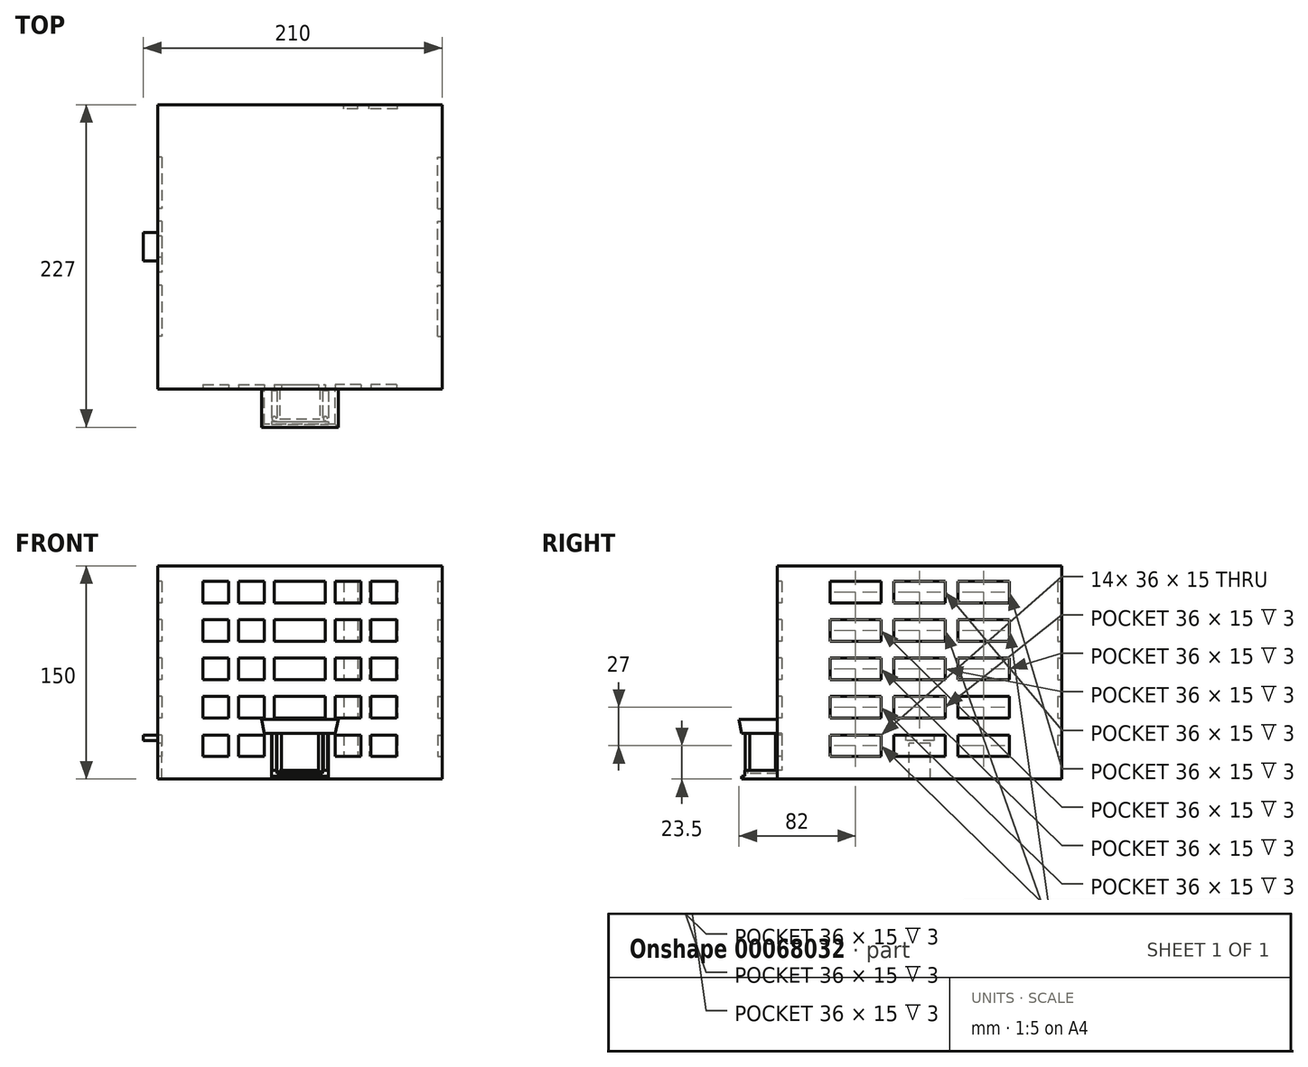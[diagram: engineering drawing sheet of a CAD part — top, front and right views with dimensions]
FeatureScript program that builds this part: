
annotation { "Feature Type Name" : "Feature", "Feature Type Description" : "" }
export const myFeature = defineFeature(function(context is Context, id is Id, definition is map)
    precondition{}
    {
        {
            var Q0;
            Q0=qCreatedBy(makeId("Top.planeOp"),FACE);
            var sketch = newSketch(context, id + "F0", { "sketchPlane" : qUnion([Q0])});
            skLineSegment(sketch, "E0.bottom", {"start": v(0, 0) * mm, "end": v(200, 0) * mm});
            skLineSegment(sketch, "E0.top", {"start": v(0, -200) * mm, "end": v(200, -200) * mm});
            skLineSegment(sketch, "E0.left", {"start": v(0, 0) * mm, "end": v(0, -200) * mm});
            skLineSegment(sketch, "E0.right", {"start": v(200, 0) * mm, "end": v(200, -200) * mm});
            skSolve(sketch);
        }
        {
            var Q0;
            Q0 = qSketchRegion(id + "F0", true);
            extrude(context, id + "F1", {"entities" : qUnion([Q0]), "depth" : 150 * mm});
        }
        {
            var Q0;
            Q0=qCreatedBy(makeId("Top.planeOp"),FACE);
            var sketch = newSketch(context, id + "F2", { "sketchPlane" : qUnion([Q0])});
            skLineSegment(sketch, "E1.bottom", {"start": v(80, -200) * mm, "end": v(120, -200) * mm});
            skLineSegment(sketch, "E1.top", {"start": v(80, -225) * mm, "end": v(120, -225) * mm});
            skLineSegment(sketch, "E1.left", {"start": v(80, -200) * mm, "end": v(80, -225) * mm});
            skLineSegment(sketch, "E1.right", {"start": v(120, -200) * mm, "end": v(120, -225) * mm});
            skSolve(sketch);
        }
        {
            var Q0;
            Q0=makeQuery(id+"F2.imprint","IMPRINT",FACE,{"disambiguationData":[TD([[makeQuery(id+"F2.imprint","IMPRINT",EDGE,{"derivedFrom":sQuery(id+"F2.wireOp",EDGE,"E1.bottom")}),-1.0]])]});
            extrude(context, id + "F3", {"entities" : qUnion([Q0]), "operationType" : NewBodyOperationType.ADD, "depth" : 2 * mm});
        }
        {
            var Q0;
            Q0=makeQuery(id+"F3.opExtrude","CAP_FACE",FACE,{"disambiguationData":[OSD([sQuery(id+"F2.wireOp",EDGE,"E1.bottom"),sQuery(id+"F2.wireOp",EDGE,"E1.top"),sQuery(id+"F2.wireOp",EDGE,"E1.left"),sQuery(id+"F2.wireOp",EDGE,"E1.right")])],"isStart":false});
            var sketch = newSketch(context, id + "F4", { "sketchPlane" : qUnion([Q0])});
            skLineSegment(sketch, "E2.bottom", {"start": v(84, -200) * mm, "end": v(116, -200) * mm});
            skLineSegment(sketch, "E2.top", {"start": v(84, -223) * mm, "end": v(116, -223) * mm});
            skLineSegment(sketch, "E2.left", {"start": v(84, -200) * mm, "end": v(84, -223) * mm});
            skLineSegment(sketch, "E2.right", {"start": v(116, -200) * mm, "end": v(116, -223) * mm});
            skSolve(sketch);
        }
        {
            var Q0;
            Q0=makeQuery(id+"F4.imprint","IMPRINT",FACE,{"disambiguationData":[TD([[makeQuery(id+"F4.imprint","IMPRINT",EDGE,{"derivedFrom":sQuery(id+"F4.wireOp",EDGE,"E2.bottom")}),-1.0]])]});
            extrude(context, id + "F5", {"entities" : qUnion([Q0]), "operationType" : NewBodyOperationType.ADD, "depth" : 2 * mm});
        }
        {
            var Q0;
            Q0=makeQuery(id+"F5.opExtrude","CAP_FACE",FACE,{"disambiguationData":[OSD([sQuery(id+"F4.wireOp",EDGE,"E2.bottom"),sQuery(id+"F4.wireOp",EDGE,"E2.top"),sQuery(id+"F4.wireOp",EDGE,"E2.left"),sQuery(id+"F4.wireOp",EDGE,"E2.right")])],"isStart":false});
            var sketch = newSketch(context, id + "F6", { "sketchPlane" : qUnion([Q0])});
            skLineSegment(sketch, "E3.bottom", {"start": v(86, -200) * mm, "end": v(114, -200) * mm});
            skLineSegment(sketch, "E3.top", {"start": v(86, -221) * mm, "end": v(114, -221) * mm});
            skLineSegment(sketch, "E3.left", {"start": v(86, -200) * mm, "end": v(86, -221) * mm});
            skLineSegment(sketch, "E3.right", {"start": v(114, -200) * mm, "end": v(114, -221) * mm});
            skSolve(sketch);
        }
        {
            var Q0;
            Q0=makeQuery(id+"F6.imprint","IMPRINT",FACE,{"disambiguationData":[TD([[makeQuery(id+"F6.imprint","IMPRINT",EDGE,{"derivedFrom":sQuery(id+"F6.wireOp",EDGE,"E3.bottom")}),-1.0]])]});
            extrude(context, id + "F7", {"entities" : qUnion([Q0]), "operationType" : NewBodyOperationType.ADD, "depth" : 2 * mm});
        }
        {
            var Q0;
            Q0=makeQuery(id+"F3.opExtrude","CAP_FACE",FACE,{"disambiguationData":[OSD([sQuery(id+"F2.wireOp",EDGE,"E1.bottom"),sQuery(id+"F2.wireOp",EDGE,"E1.top"),sQuery(id+"F2.wireOp",EDGE,"E1.left"),sQuery(id+"F2.wireOp",EDGE,"E1.right")])],"isStart":false});
            var sketch = newSketch(context, id + "F8", { "sketchPlane" : qUnion([Q0])});
            skLineSegment(sketch, "E4.bottom", {"start": v(84, -223) * mm, "end": v(80, -223) * mm});
            skLineSegment(sketch, "E4.top", {"start": v(84, -200) * mm, "end": v(80, -200) * mm});
            skLineSegment(sketch, "E4.left", {"start": v(84, -223) * mm, "end": v(84, -200) * mm});
            skLineSegment(sketch, "E4.right", {"start": v(80, -223) * mm, "end": v(80, -200) * mm});
            skLineSegment(sketch, "E5.bottom", {"start": v(116, -200) * mm, "end": v(120, -200) * mm});
            skLineSegment(sketch, "E5.top", {"start": v(116, -223) * mm, "end": v(120, -223) * mm});
            skLineSegment(sketch, "E5.left", {"start": v(116, -200) * mm, "end": v(116, -223) * mm});
            skLineSegment(sketch, "E5.right", {"start": v(120, -200) * mm, "end": v(120, -223) * mm});
            skSolve(sketch);
        }
        {
            var Q0;
            Q0 = qSketchRegion(id + "F8", true);
            extrude(context, id + "F9", {"entities" : qUnion([Q0]), "operationType" : NewBodyOperationType.ADD, "depth" : 4 * mm});
        }
        {
            var Q0;
            Q0=makeQuery(id+"F9.opExtrude","CAP_FACE",FACE,{"disambiguationData":[OSD([sQuery(id+"F8.wireOp",EDGE,"E4.bottom"),sQuery(id+"F8.wireOp",EDGE,"E4.top"),sQuery(id+"F8.wireOp",EDGE,"E4.left"),sQuery(id+"F8.wireOp",EDGE,"E4.right")])],"isStart":false});
            var sketch = newSketch(context, id + "F10", { "sketchPlane" : qUnion([Q0])});
            skCircle(sketch, "E6", {"center": v(82, -221) * mm, "radius": 1.5 * mm});
            skCircle(sketch, "E7", {"center": v(118, -221) * mm, "radius": 1.5 * mm});
            skSolve(sketch);
        }
        {
            var Q0;
            Q0 = qSketchRegion(id + "F10", true);
            extrude(context, id + "F11", {"entities" : qUnion([Q0]), "operationType" : NewBodyOperationType.ADD, "depth" : 26 * mm});
        }
        {
            var Q0;
            Q0=makeQuery(id+"F11.opExtrude","CAP_FACE",FACE,{"disambiguationData":[OSD([sQuery(id+"F10.wireOp",EDGE,"E7")])],"isStart":false});
            var sketch = newSketch(context, id + "F12", { "sketchPlane" : qUnion([Q0])});
            skLineSegment(sketch, "E8.bottom", {"start": v(125, -225) * mm, "end": v(75, -225) * mm});
            skLineSegment(sketch, "E8.top", {"start": v(125, -200) * mm, "end": v(75, -200) * mm});
            skLineSegment(sketch, "E8.left", {"start": v(125, -225) * mm, "end": v(125, -200) * mm});
            skLineSegment(sketch, "E8.right", {"start": v(75, -225) * mm, "end": v(75, -200) * mm});
            skSolve(sketch);
        }
        {
            var Q0;
            Q0=makeQuery(id+"F12.imprint","IMPRINT",FACE,{"disambiguationData":[TD([[makeQuery(id+"F12.imprint","IMPRINT",EDGE,{"derivedFrom":sQuery(id+"F12.wireOp",EDGE,"E8.bottom")}),-1.0]])]});
            cPlane(context, id + "F13", {"entities" : qUnion([Q0]), "cplaneType" : CPlaneType.OFFSET, "offset" : 10 * mm, "width" : 150 * mm, "height" : 150 * mm});
        }
        {
            var Q0;
            Q0=qCreatedBy(id+"F13.planeOp",FACE);
            var sketch = newSketch(context, id + "F14", { "sketchPlane" : qUnion([Q0])});
            skLineSegment(sketch, "E9.bottom", {"start": v(73, -200) * mm, "end": v(127, -200) * mm});
            skLineSegment(sketch, "E9.top", {"start": v(73, -227) * mm, "end": v(127, -227) * mm});
            skLineSegment(sketch, "E9.left", {"start": v(73, -200) * mm, "end": v(73, -227) * mm});
            skLineSegment(sketch, "E9.right", {"start": v(127, -200) * mm, "end": v(127, -227) * mm});
            skSolve(sketch);
        }
        {
            var Q1;
            Q1 = qSketchRegion(id + "F14", true);
            var Q2;
            Q2 = qSketchRegion(id + "F12", true);
            loft(context, id + "F15", {"operationType" : NewBodyOperationType.ADD, "sheetProfilesArray" : [{ "sheetProfileEntities" : qUnion([Q1]) }, { "sheetProfileEntities" : qUnion([Q2]) }]});
        }
        {
            var Q0;
            Q0=makeQuery(id+"F1.opExtrude","SWEPT_FACE",FACE,{"disambiguationData":[OSD([sQuery(id+"F0.wireOp",EDGE,"E0.top")])]});
            var sketch = newSketch(context, id + "F16", { "sketchPlane" : qUnion([Q0])});
            skLineSegment(sketch, "E10.bottom", {"start": v(84, 6) * mm, "end": v(80, 6) * mm});
            skLineSegment(sketch, "E10.top", {"start": v(84, 32) * mm, "end": v(80, 32) * mm});
            skLineSegment(sketch, "E10.left", {"start": v(84, 6) * mm, "end": v(84, 32) * mm});
            skLineSegment(sketch, "E10.right", {"start": v(80, 6) * mm, "end": v(80, 32) * mm});
            skLineSegment(sketch, "E11.bottom", {"start": v(116, 6) * mm, "end": v(120, 6) * mm});
            skLineSegment(sketch, "E11.top", {"start": v(116, 32) * mm, "end": v(120, 32) * mm});
            skLineSegment(sketch, "E11.left", {"start": v(116, 6) * mm, "end": v(116, 32) * mm});
            skLineSegment(sketch, "E11.right", {"start": v(120, 6) * mm, "end": v(120, 32) * mm});
            skSolve(sketch);
        }
        {
            var Q0;
            Q0 = qSketchRegion(id + "F16", true);
            extrude(context, id + "F17", {"entities" : qUnion([Q0]), "operationType" : NewBodyOperationType.ADD, "depth" : 1.5 * mm});
        }
        {
            var Q0;
            {var subQ7=sQuery(id+"F0.wireOp",EDGE,"E0.left");var subQ11=sQuery(id+"F0.wireOp",EDGE,"E0.top");Q0=makeQuery(id+"F17.boolean.opBoolean","SPLIT",FACE,{"disambiguationData":[TD([makeQuery(id+"F1.opExtrude","SWEPT_FACE",FACE,{"disambiguationData":[OSD([subQ7])]})])],"derivedFrom":makeQuery(id+"F1.opExtrude","SWEPT_FACE",FACE,{"disambiguationData":[OSD([subQ11])]})});}
            var sketch = newSketch(context, id + "F18", { "sketchPlane" : qUnion([Q0])});
            skLineSegment(sketch, "E12.bottom", {"start": v(32, 139) * mm, "end": v(50, 139) * mm});
            skLineSegment(sketch, "E12.top", {"start": v(32, 124) * mm, "end": v(50, 124) * mm});
            skLineSegment(sketch, "E12.left", {"start": v(32, 139) * mm, "end": v(32, 124) * mm});
            skLineSegment(sketch, "E12.right", {"start": v(50, 139) * mm, "end": v(50, 124) * mm});
            skLineSegment(sketch, "E13.0.1.0", {"start": v(32, 112) * mm, "end": v(50, 112) * mm});
            skLineSegment(sketch, "E13.0.1.1", {"start": v(32, 97) * mm, "end": v(50, 97) * mm});
            skLineSegment(sketch, "E13.0.1.2", {"start": v(32, 112) * mm, "end": v(32, 97) * mm});
            skLineSegment(sketch, "E13.0.1.3", {"start": v(50, 112) * mm, "end": v(50, 97) * mm});
            skLineSegment(sketch, "E13.0.2.0", {"start": v(32, 85) * mm, "end": v(50, 85) * mm});
            skLineSegment(sketch, "E13.0.2.1", {"start": v(32, 70) * mm, "end": v(50, 70) * mm});
            skLineSegment(sketch, "E13.0.2.2", {"start": v(32, 85) * mm, "end": v(32, 70) * mm});
            skLineSegment(sketch, "E13.0.2.3", {"start": v(50, 85) * mm, "end": v(50, 70) * mm});
            skLineSegment(sketch, "E13.0.3.0", {"start": v(32, 58) * mm, "end": v(50, 58) * mm});
            skLineSegment(sketch, "E13.0.3.1", {"start": v(32, 43) * mm, "end": v(50, 43) * mm});
            skLineSegment(sketch, "E13.0.3.2", {"start": v(32, 58) * mm, "end": v(32, 43) * mm});
            skLineSegment(sketch, "E13.0.3.3", {"start": v(50, 58) * mm, "end": v(50, 43) * mm});
            skLineSegment(sketch, "E13.0.4.0", {"start": v(32, 31) * mm, "end": v(50, 31) * mm});
            skLineSegment(sketch, "E13.0.4.1", {"start": v(32, 16) * mm, "end": v(50, 16) * mm});
            skLineSegment(sketch, "E13.0.4.2", {"start": v(32, 31) * mm, "end": v(32, 16) * mm});
            skLineSegment(sketch, "E13.0.4.3", {"start": v(50, 31) * mm, "end": v(50, 16) * mm});
            skLineSegment(sketch, "E13.1.0.0", {"start": v(57, 139) * mm, "end": v(75, 139) * mm});
            skLineSegment(sketch, "E13.1.0.1", {"start": v(57, 124) * mm, "end": v(75, 124) * mm});
            skLineSegment(sketch, "E13.1.0.2", {"start": v(57, 139) * mm, "end": v(57, 124) * mm});
            skLineSegment(sketch, "E13.1.0.3", {"start": v(75, 139) * mm, "end": v(75, 124) * mm});
            skLineSegment(sketch, "E13.1.1.0", {"start": v(57, 112) * mm, "end": v(75, 112) * mm});
            skLineSegment(sketch, "E13.1.1.1", {"start": v(57, 97) * mm, "end": v(75, 97) * mm});
            skLineSegment(sketch, "E13.1.1.2", {"start": v(57, 112) * mm, "end": v(57, 97) * mm});
            skLineSegment(sketch, "E13.1.1.3", {"start": v(75, 112) * mm, "end": v(75, 97) * mm});
            skLineSegment(sketch, "E13.1.2.0", {"start": v(57, 85) * mm, "end": v(75, 85) * mm});
            skLineSegment(sketch, "E13.1.2.1", {"start": v(57, 70) * mm, "end": v(75, 70) * mm});
            skLineSegment(sketch, "E13.1.2.2", {"start": v(57, 85) * mm, "end": v(57, 70) * mm});
            skLineSegment(sketch, "E13.1.2.3", {"start": v(75, 85) * mm, "end": v(75, 70) * mm});
            skLineSegment(sketch, "E13.1.3.0", {"start": v(57, 58) * mm, "end": v(75, 58) * mm});
            skLineSegment(sketch, "E13.1.3.1", {"start": v(57, 43) * mm, "end": v(75, 43) * mm});
            skLineSegment(sketch, "E13.1.3.2", {"start": v(57, 58) * mm, "end": v(57, 43) * mm});
            skLineSegment(sketch, "E13.1.3.3", {"start": v(75, 58) * mm, "end": v(75, 43) * mm});
            skLineSegment(sketch, "E13.1.4.0", {"start": v(57, 31) * mm, "end": v(75, 31) * mm});
            skLineSegment(sketch, "E13.1.4.1", {"start": v(57, 16) * mm, "end": v(75, 16) * mm});
            skLineSegment(sketch, "E13.1.4.2", {"start": v(57, 31) * mm, "end": v(57, 16) * mm});
            skLineSegment(sketch, "E13.1.4.3", {"start": v(75, 31) * mm, "end": v(75, 16) * mm});
            skLineSegment(sketch, "E13.2.0.0", {"start": v(82, 139) * mm, "end": v(100, 139) * mm});
            skLineSegment(sketch, "E13.2.0.1", {"start": v(82, 124) * mm, "end": v(100, 124) * mm});
            skLineSegment(sketch, "E13.2.0.2", {"start": v(82, 139) * mm, "end": v(82, 124) * mm});
            skLineSegment(sketch, "E13.2.0.3", {"start": v(100, 139) * mm, "end": v(100, 124) * mm});
            skLineSegment(sketch, "E13.2.1.0", {"start": v(82, 112) * mm, "end": v(100, 112) * mm});
            skLineSegment(sketch, "E13.2.1.1", {"start": v(82, 97) * mm, "end": v(100, 97) * mm});
            skLineSegment(sketch, "E13.2.1.2", {"start": v(82, 112) * mm, "end": v(82, 97) * mm});
            skLineSegment(sketch, "E13.2.1.3", {"start": v(100, 112) * mm, "end": v(100, 97) * mm});
            skLineSegment(sketch, "E13.2.2.0", {"start": v(82, 85) * mm, "end": v(100, 85) * mm});
            skLineSegment(sketch, "E13.2.2.1", {"start": v(82, 70) * mm, "end": v(100, 70) * mm});
            skLineSegment(sketch, "E13.2.2.2", {"start": v(82, 85) * mm, "end": v(82, 70) * mm});
            skLineSegment(sketch, "E13.2.2.3", {"start": v(100, 85) * mm, "end": v(100, 70) * mm});
            skLineSegment(sketch, "E13.2.3.0", {"start": v(82, 58) * mm, "end": v(100, 58) * mm});
            skLineSegment(sketch, "E13.2.3.1", {"start": v(82, 43) * mm, "end": v(100, 43) * mm});
            skLineSegment(sketch, "E13.2.3.2", {"start": v(82, 58) * mm, "end": v(82, 43) * mm});
            skLineSegment(sketch, "E13.2.3.3", {"start": v(100, 58) * mm, "end": v(100, 43) * mm});
            skLineSegment(sketch, "E13.direction1", {"start": v(32, 139) * mm, "end": v(57, 139) * mm, "construction": true});
            skLineSegment(sketch, "E13.direction2", {"start": v(32, 139) * mm, "end": v(32, 112) * mm, "construction": true});
            skLineSegment(sketch, "E14", {"start": v(100, 150) * mm, "end": v(100, -27.9) * mm, "construction": true});
            skLineSegment(sketch, "E15.MirrorCS", {"start": v(125, 85) * mm, "end": v(125, 70) * mm});
            skLineSegment(sketch, "E16.MirrorCS", {"start": v(118, 58) * mm, "end": v(118, 43) * mm});
            skLineSegment(sketch, "E17.MirrorCS", {"start": v(143, 31) * mm, "end": v(143, 16) * mm});
            skLineSegment(sketch, "E18.MirrorCS", {"start": v(143, 139) * mm, "end": v(143, 124) * mm});
            skLineSegment(sketch, "E19.MirrorCS", {"start": v(143, 85) * mm, "end": v(125, 85) * mm});
            skLineSegment(sketch, "E20.MirrorCS", {"start": v(118, 112) * mm, "end": v(100, 112) * mm});
            skLineSegment(sketch, "E21.MirrorCS", {"start": v(168, 58) * mm, "end": v(150, 58) * mm});
            skLineSegment(sketch, "E22.MirrorCS", {"start": v(150, 85) * mm, "end": v(150, 70) * mm});
            skLineSegment(sketch, "E23.MirrorCS", {"start": v(168, 85) * mm, "end": v(168, 70) * mm});
            skLineSegment(sketch, "E24.MirrorCS", {"start": v(168, 70) * mm, "end": v(150, 70) * mm});
            skLineSegment(sketch, "E25.MirrorCS", {"start": v(168, 85) * mm, "end": v(150, 85) * mm});
            skLineSegment(sketch, "E26.MirrorCS", {"start": v(150, 112) * mm, "end": v(150, 97) * mm});
            skLineSegment(sketch, "E27.MirrorCS", {"start": v(168, 112) * mm, "end": v(168, 97) * mm});
            skLineSegment(sketch, "E28.MirrorCS", {"start": v(168, 97) * mm, "end": v(150, 97) * mm});
            skLineSegment(sketch, "E29.MirrorCS", {"start": v(168, 112) * mm, "end": v(150, 112) * mm});
            skLineSegment(sketch, "E30.MirrorCS", {"start": v(150, 139) * mm, "end": v(150, 124) * mm});
            skLineSegment(sketch, "E31.MirrorCS", {"start": v(168, 139) * mm, "end": v(168, 124) * mm});
            skLineSegment(sketch, "E32.MirrorCS", {"start": v(168, 124) * mm, "end": v(150, 124) * mm});
            skLineSegment(sketch, "E33.MirrorCS", {"start": v(150, 58) * mm, "end": v(150, 43) * mm});
            skLineSegment(sketch, "E34.MirrorCS", {"start": v(168, 139) * mm, "end": v(150, 139) * mm});
            skLineSegment(sketch, "E35.MirrorCS", {"start": v(143, 16) * mm, "end": v(125, 16) * mm});
            skLineSegment(sketch, "E36.MirrorCS", {"start": v(143, 85) * mm, "end": v(143, 70) * mm});
            skLineSegment(sketch, "E37.MirrorCS", {"start": v(118, 112) * mm, "end": v(118, 97) * mm});
            skLineSegment(sketch, "E38.MirrorCS", {"start": v(118, 43) * mm, "end": v(100, 43) * mm});
            skLineSegment(sketch, "E39.MirrorCS", {"start": v(168, 58) * mm, "end": v(168, 43) * mm});
            skLineSegment(sketch, "E40.MirrorCS", {"start": v(143, 124) * mm, "end": v(125, 124) * mm});
            skLineSegment(sketch, "E41.MirrorCS", {"start": v(125, 112) * mm, "end": v(125, 97) * mm});
            skLineSegment(sketch, "E42.MirrorCS", {"start": v(168, 43) * mm, "end": v(150, 43) * mm});
            skLineSegment(sketch, "E43.MirrorCS", {"start": v(143, 70) * mm, "end": v(125, 70) * mm});
            skLineSegment(sketch, "E44.MirrorCS", {"start": v(143, 31) * mm, "end": v(125, 31) * mm});
            skLineSegment(sketch, "E45.MirrorCS", {"start": v(118, 58) * mm, "end": v(100, 58) * mm});
            skLineSegment(sketch, "E46.MirrorCS", {"start": v(118, 97) * mm, "end": v(100, 97) * mm});
            skLineSegment(sketch, "E47.MirrorCS", {"start": v(143, 112) * mm, "end": v(143, 97) * mm});
            skLineSegment(sketch, "E48.MirrorCS", {"start": v(143, 139) * mm, "end": v(125, 139) * mm});
            skLineSegment(sketch, "E49.MirrorCS", {"start": v(118, 139) * mm, "end": v(118, 124) * mm});
            skLineSegment(sketch, "E50.MirrorCS", {"start": v(125, 58) * mm, "end": v(125, 43) * mm});
            skLineSegment(sketch, "E51.MirrorCS", {"start": v(150, 31) * mm, "end": v(150, 16) * mm});
            skLineSegment(sketch, "E52.MirrorCS", {"start": v(143, 97) * mm, "end": v(125, 97) * mm});
            skLineSegment(sketch, "E53.MirrorCS", {"start": v(168, 139) * mm, "end": v(168, 112) * mm, "construction": true});
            skLineSegment(sketch, "E54.MirrorCS", {"start": v(118, 124) * mm, "end": v(100, 124) * mm});
            skLineSegment(sketch, "E55.MirrorCS", {"start": v(143, 58) * mm, "end": v(143, 43) * mm});
            skLineSegment(sketch, "E56.MirrorCS", {"start": v(118, 85) * mm, "end": v(118, 70) * mm});
            skLineSegment(sketch, "E57.MirrorCS", {"start": v(168, 31) * mm, "end": v(168, 16) * mm});
            skLineSegment(sketch, "E58.MirrorCS", {"start": v(143, 112) * mm, "end": v(125, 112) * mm});
            skLineSegment(sketch, "E59.MirrorCS", {"start": v(118, 139) * mm, "end": v(100, 139) * mm});
            skLineSegment(sketch, "E60.MirrorCS", {"start": v(168, 139) * mm, "end": v(143, 139) * mm, "construction": true});
            skLineSegment(sketch, "E61.MirrorCS", {"start": v(143, 43) * mm, "end": v(125, 43) * mm});
            skLineSegment(sketch, "E62.MirrorCS", {"start": v(118, 70) * mm, "end": v(100, 70) * mm});
            skLineSegment(sketch, "E63.MirrorCS", {"start": v(168, 16) * mm, "end": v(150, 16) * mm});
            skLineSegment(sketch, "E64.MirrorCS", {"start": v(143, 58) * mm, "end": v(125, 58) * mm});
            skLineSegment(sketch, "E65.MirrorCS", {"start": v(118, 85) * mm, "end": v(100, 85) * mm});
            skLineSegment(sketch, "E66.MirrorCS", {"start": v(125, 139) * mm, "end": v(125, 124) * mm});
            skLineSegment(sketch, "E67.MirrorCS", {"start": v(168, 31) * mm, "end": v(150, 31) * mm});
            skLineSegment(sketch, "E68.MirrorCS", {"start": v(125, 31) * mm, "end": v(125, 16) * mm});
            skLineSegment(sketch, "E69.bottom", {"start": v(87, 32) * mm, "end": v(113, 32) * mm});
            skLineSegment(sketch, "E69.top", {"start": v(87, 6) * mm, "end": v(113, 6) * mm});
            skLineSegment(sketch, "E69.left", {"start": v(87, 32) * mm, "end": v(87, 6) * mm});
            skLineSegment(sketch, "E69.right", {"start": v(113, 32) * mm, "end": v(113, 6) * mm});
            skSolve(sketch);
        }
        {
            var Q0;
            Q0 = qSketchRegion(id + "F18", true);
            extrude(context, id + "F19", {"entities" : qUnion([Q0]), "operationType" : NewBodyOperationType.REMOVE, "oppositeDirection" : true, "depth" : 3 * mm});
        }
        {
            var Q0;
            Q0=makeQuery(id+"F1.opExtrude","SWEPT_FACE",FACE,{"disambiguationData":[OSD([sQuery(id+"F0.wireOp",EDGE,"E0.right")])]});
            var sketch = newSketch(context, id + "F20", { "sketchPlane" : qUnion([Q0])});
            skLineSegment(sketch, "E70.bottom", {"start": v(-163, 139) * mm, "end": v(-127, 139) * mm});
            skLineSegment(sketch, "E70.top", {"start": v(-163, 124) * mm, "end": v(-127, 124) * mm});
            skLineSegment(sketch, "E70.left", {"start": v(-163, 139) * mm, "end": v(-163, 124) * mm});
            skLineSegment(sketch, "E70.right", {"start": v(-127, 139) * mm, "end": v(-127, 124) * mm});
            skLineSegment(sketch, "E71.direction1", {"start": v(-127, 124) * mm, "end": v(-82, 124) * mm, "construction": true});
            skLineSegment(sketch, "E72.0.1.0", {"start": v(-82, 139) * mm, "end": v(-82, 124) * mm});
            skLineSegment(sketch, "E72.3.1.0", {"start": v(-118, 139) * mm, "end": v(-118, 124) * mm});
            skLineSegment(sketch, "E72.6.1.0", {"start": v(-118, 124) * mm, "end": v(-82, 124) * mm});
            skLineSegment(sketch, "E72.9.1.0", {"start": v(-118, 139) * mm, "end": v(-82, 139) * mm});
            skLineSegment(sketch, "E72.0.2.0", {"start": v(-37, 139) * mm, "end": v(-37, 124) * mm});
            skLineSegment(sketch, "E72.3.2.0", {"start": v(-73, 139) * mm, "end": v(-73, 124) * mm});
            skLineSegment(sketch, "E72.6.2.0", {"start": v(-73, 124) * mm, "end": v(-37, 124) * mm});
            skLineSegment(sketch, "E72.9.2.0", {"start": v(-73, 139) * mm, "end": v(-37, 139) * mm});
            skLineSegment(sketch, "E73.0.1.0", {"start": v(-127, 112) * mm, "end": v(-127, 97) * mm});
            skLineSegment(sketch, "E73.0.1.1", {"start": v(-163, 112) * mm, "end": v(-163, 97) * mm});
            skLineSegment(sketch, "E73.0.1.2", {"start": v(-163, 97) * mm, "end": v(-127, 97) * mm});
            skLineSegment(sketch, "E73.0.1.3", {"start": v(-163, 112) * mm, "end": v(-127, 112) * mm});
            skLineSegment(sketch, "E73.0.1.4", {"start": v(-127, 97) * mm, "end": v(-82, 97) * mm, "construction": true});
            skLineSegment(sketch, "E73.0.2.0", {"start": v(-127, 85) * mm, "end": v(-127, 70) * mm});
            skLineSegment(sketch, "E73.0.2.1", {"start": v(-163, 85) * mm, "end": v(-163, 70) * mm});
            skLineSegment(sketch, "E73.0.2.2", {"start": v(-163, 70) * mm, "end": v(-127, 70) * mm});
            skLineSegment(sketch, "E73.0.2.3", {"start": v(-163, 85) * mm, "end": v(-127, 85) * mm});
            skLineSegment(sketch, "E73.0.2.4", {"start": v(-127, 70) * mm, "end": v(-82, 70) * mm, "construction": true});
            skLineSegment(sketch, "E73.0.3.0", {"start": v(-127, 58) * mm, "end": v(-127, 43) * mm});
            skLineSegment(sketch, "E73.0.3.1", {"start": v(-163, 58) * mm, "end": v(-163, 43) * mm});
            skLineSegment(sketch, "E73.0.3.2", {"start": v(-163, 43) * mm, "end": v(-127, 43) * mm});
            skLineSegment(sketch, "E73.0.3.3", {"start": v(-163, 58) * mm, "end": v(-127, 58) * mm});
            skLineSegment(sketch, "E73.0.3.4", {"start": v(-127, 43) * mm, "end": v(-82, 43) * mm, "construction": true});
            skLineSegment(sketch, "E73.0.4.0", {"start": v(-127, 31) * mm, "end": v(-127, 16) * mm});
            skLineSegment(sketch, "E73.0.4.1", {"start": v(-163, 31) * mm, "end": v(-163, 16) * mm});
            skLineSegment(sketch, "E73.0.4.2", {"start": v(-163, 16) * mm, "end": v(-127, 16) * mm});
            skLineSegment(sketch, "E73.0.4.3", {"start": v(-163, 31) * mm, "end": v(-127, 31) * mm});
            skLineSegment(sketch, "E73.0.4.4", {"start": v(-127, 16) * mm, "end": v(-82, 16) * mm, "construction": true});
            skLineSegment(sketch, "E73.direction1", {"start": v(-118, 139) * mm, "end": v(-93, 139) * mm, "construction": true});
            skLineSegment(sketch, "E73.direction2", {"start": v(-118, 139) * mm, "end": v(-118, 112) * mm, "construction": true});
            skLineSegment(sketch, "E74.0.1.0", {"start": v(-118, 97) * mm, "end": v(-82, 97) * mm});
            skLineSegment(sketch, "E74.0.1.1", {"start": v(-118, 112) * mm, "end": v(-118, 97) * mm});
            skLineSegment(sketch, "E74.0.1.2", {"start": v(-82, 112) * mm, "end": v(-82, 97) * mm});
            skLineSegment(sketch, "E74.0.1.3", {"start": v(-73, 97) * mm, "end": v(-37, 97) * mm});
            skLineSegment(sketch, "E74.0.1.4", {"start": v(-73, 112) * mm, "end": v(-73, 97) * mm});
            skLineSegment(sketch, "E74.0.1.5", {"start": v(-37, 112) * mm, "end": v(-37, 97) * mm});
            skLineSegment(sketch, "E74.0.1.6", {"start": v(-73, 112) * mm, "end": v(-37, 112) * mm});
            skLineSegment(sketch, "E74.0.1.7", {"start": v(-118, 112) * mm, "end": v(-82, 112) * mm});
            skLineSegment(sketch, "E74.0.1.8", {"start": v(-118, 112) * mm, "end": v(-93, 112) * mm, "construction": true});
            skLineSegment(sketch, "E74.0.2.0", {"start": v(-118, 70) * mm, "end": v(-82, 70) * mm});
            skLineSegment(sketch, "E74.0.2.1", {"start": v(-118, 85) * mm, "end": v(-118, 70) * mm});
            skLineSegment(sketch, "E74.0.2.2", {"start": v(-82, 85) * mm, "end": v(-82, 70) * mm});
            skLineSegment(sketch, "E74.0.2.3", {"start": v(-73, 70) * mm, "end": v(-37, 70) * mm});
            skLineSegment(sketch, "E74.0.2.4", {"start": v(-73, 85) * mm, "end": v(-73, 70) * mm});
            skLineSegment(sketch, "E74.0.2.5", {"start": v(-37, 85) * mm, "end": v(-37, 70) * mm});
            skLineSegment(sketch, "E74.0.2.6", {"start": v(-73, 85) * mm, "end": v(-37, 85) * mm});
            skLineSegment(sketch, "E74.0.2.7", {"start": v(-118, 85) * mm, "end": v(-82, 85) * mm});
            skLineSegment(sketch, "E74.0.2.8", {"start": v(-118, 85) * mm, "end": v(-93, 85) * mm, "construction": true});
            skLineSegment(sketch, "E74.0.3.0", {"start": v(-118, 43) * mm, "end": v(-82, 43) * mm});
            skLineSegment(sketch, "E74.0.3.1", {"start": v(-118, 58) * mm, "end": v(-118, 43) * mm});
            skLineSegment(sketch, "E74.0.3.2", {"start": v(-82, 58) * mm, "end": v(-82, 43) * mm});
            skLineSegment(sketch, "E74.0.3.3", {"start": v(-73, 43) * mm, "end": v(-37, 43) * mm});
            skLineSegment(sketch, "E74.0.3.4", {"start": v(-73, 58) * mm, "end": v(-73, 43) * mm});
            skLineSegment(sketch, "E74.0.3.5", {"start": v(-37, 58) * mm, "end": v(-37, 43) * mm});
            skLineSegment(sketch, "E74.0.3.6", {"start": v(-73, 58) * mm, "end": v(-37, 58) * mm});
            skLineSegment(sketch, "E74.0.3.7", {"start": v(-118, 58) * mm, "end": v(-82, 58) * mm});
            skLineSegment(sketch, "E74.0.3.8", {"start": v(-118, 58) * mm, "end": v(-93, 58) * mm, "construction": true});
            skLineSegment(sketch, "E74.0.4.0", {"start": v(-118, 16) * mm, "end": v(-82, 16) * mm});
            skLineSegment(sketch, "E74.0.4.1", {"start": v(-118, 31) * mm, "end": v(-118, 16) * mm});
            skLineSegment(sketch, "E74.0.4.2", {"start": v(-82, 31) * mm, "end": v(-82, 16) * mm});
            skLineSegment(sketch, "E74.0.4.3", {"start": v(-73, 16) * mm, "end": v(-37, 16) * mm});
            skLineSegment(sketch, "E74.0.4.4", {"start": v(-73, 31) * mm, "end": v(-73, 16) * mm});
            skLineSegment(sketch, "E74.0.4.5", {"start": v(-37, 31) * mm, "end": v(-37, 16) * mm});
            skLineSegment(sketch, "E74.0.4.6", {"start": v(-73, 31) * mm, "end": v(-37, 31) * mm});
            skLineSegment(sketch, "E74.0.4.7", {"start": v(-118, 31) * mm, "end": v(-82, 31) * mm});
            skLineSegment(sketch, "E74.0.4.8", {"start": v(-118, 31) * mm, "end": v(-93, 31) * mm, "construction": true});
            skLineSegment(sketch, "E74.direction1", {"start": v(-118, 124) * mm, "end": v(-93, 124) * mm, "construction": true});
            skLineSegment(sketch, "E74.direction2", {"start": v(-118, 124) * mm, "end": v(-118, 97) * mm, "construction": true});
            skSolve(sketch);
        }
        {
            var Q0;
            Q0 = qSketchRegion(id + "F20", true);
            extrude(context, id + "F21", {"entities" : qUnion([Q0]), "operationType" : NewBodyOperationType.REMOVE, "oppositeDirection" : true, "depth" : 3 * mm});
        }
        {
            var Q0;
            Q0=makeQuery(id+"F1.opExtrude","SWEPT_FACE",FACE,{"disambiguationData":[OSD([sQuery(id+"F0.wireOp",EDGE,"E0.left")])]});
            var sketch = newSketch(context, id + "F22", { "sketchPlane" : qUnion([Q0])});
            skLineSegment(sketch, "E75.bottom", {"start": v(37, 139) * mm, "end": v(73, 139) * mm});
            skLineSegment(sketch, "E75.top", {"start": v(37, 124) * mm, "end": v(73, 124) * mm});
            skLineSegment(sketch, "E75.left", {"start": v(37, 139) * mm, "end": v(37, 124) * mm});
            skLineSegment(sketch, "E75.right", {"start": v(73, 139) * mm, "end": v(73, 124) * mm});
            skLineSegment(sketch, "E76.0.1.0", {"start": v(37, 112) * mm, "end": v(73, 112) * mm});
            skLineSegment(sketch, "E76.0.1.1", {"start": v(37, 97) * mm, "end": v(73, 97) * mm});
            skLineSegment(sketch, "E76.0.1.2", {"start": v(37, 112) * mm, "end": v(37, 97) * mm});
            skLineSegment(sketch, "E76.0.1.3", {"start": v(73, 112) * mm, "end": v(73, 97) * mm});
            skLineSegment(sketch, "E76.0.2.0", {"start": v(37, 85) * mm, "end": v(73, 85) * mm});
            skLineSegment(sketch, "E76.0.2.1", {"start": v(37, 70) * mm, "end": v(73, 70) * mm});
            skLineSegment(sketch, "E76.0.2.2", {"start": v(37, 85) * mm, "end": v(37, 70) * mm});
            skLineSegment(sketch, "E76.0.2.3", {"start": v(73, 85) * mm, "end": v(73, 70) * mm});
            skLineSegment(sketch, "E76.0.3.0", {"start": v(37, 58) * mm, "end": v(73, 58) * mm});
            skLineSegment(sketch, "E76.0.3.1", {"start": v(37, 43) * mm, "end": v(73, 43) * mm});
            skLineSegment(sketch, "E76.0.3.2", {"start": v(37, 58) * mm, "end": v(37, 43) * mm});
            skLineSegment(sketch, "E76.0.3.3", {"start": v(73, 58) * mm, "end": v(73, 43) * mm});
            skLineSegment(sketch, "E76.0.4.0", {"start": v(37, 31) * mm, "end": v(73, 31) * mm});
            skLineSegment(sketch, "E76.0.4.1", {"start": v(37, 16) * mm, "end": v(73, 16) * mm});
            skLineSegment(sketch, "E76.0.4.2", {"start": v(37, 31) * mm, "end": v(37, 16) * mm});
            skLineSegment(sketch, "E76.0.4.3", {"start": v(73, 31) * mm, "end": v(73, 16) * mm});
            skLineSegment(sketch, "E76.1.0.0", {"start": v(82, 139) * mm, "end": v(118, 139) * mm});
            skLineSegment(sketch, "E76.1.0.1", {"start": v(82, 124) * mm, "end": v(118, 124) * mm});
            skLineSegment(sketch, "E76.1.0.2", {"start": v(82, 139) * mm, "end": v(82, 124) * mm});
            skLineSegment(sketch, "E76.1.0.3", {"start": v(118, 139) * mm, "end": v(118, 124) * mm});
            skLineSegment(sketch, "E76.1.1.0", {"start": v(82, 112) * mm, "end": v(118, 112) * mm});
            skLineSegment(sketch, "E76.1.1.1", {"start": v(82, 97) * mm, "end": v(118, 97) * mm});
            skLineSegment(sketch, "E76.1.1.2", {"start": v(82, 112) * mm, "end": v(82, 97) * mm});
            skLineSegment(sketch, "E76.1.1.3", {"start": v(118, 112) * mm, "end": v(118, 97) * mm});
            skLineSegment(sketch, "E76.1.2.0", {"start": v(82, 85) * mm, "end": v(118, 85) * mm});
            skLineSegment(sketch, "E76.1.2.1", {"start": v(82, 70) * mm, "end": v(118, 70) * mm});
            skLineSegment(sketch, "E76.1.2.2", {"start": v(82, 85) * mm, "end": v(82, 70) * mm});
            skLineSegment(sketch, "E76.1.2.3", {"start": v(118, 85) * mm, "end": v(118, 70) * mm});
            skLineSegment(sketch, "E76.1.3.0", {"start": v(82, 58) * mm, "end": v(118, 58) * mm});
            skLineSegment(sketch, "E76.1.3.1", {"start": v(82, 43) * mm, "end": v(118, 43) * mm});
            skLineSegment(sketch, "E76.1.3.2", {"start": v(82, 58) * mm, "end": v(82, 43) * mm});
            skLineSegment(sketch, "E76.1.3.3", {"start": v(118, 58) * mm, "end": v(118, 43) * mm});
            skLineSegment(sketch, "E76.2.0.0", {"start": v(127, 139) * mm, "end": v(163, 139) * mm});
            skLineSegment(sketch, "E76.2.0.1", {"start": v(127, 124) * mm, "end": v(163, 124) * mm});
            skLineSegment(sketch, "E76.2.0.2", {"start": v(127, 139) * mm, "end": v(127, 124) * mm});
            skLineSegment(sketch, "E76.2.0.3", {"start": v(163, 139) * mm, "end": v(163, 124) * mm});
            skLineSegment(sketch, "E76.2.1.0", {"start": v(127, 112) * mm, "end": v(163, 112) * mm});
            skLineSegment(sketch, "E76.2.1.1", {"start": v(127, 97) * mm, "end": v(163, 97) * mm});
            skLineSegment(sketch, "E76.2.1.2", {"start": v(127, 112) * mm, "end": v(127, 97) * mm});
            skLineSegment(sketch, "E76.2.1.3", {"start": v(163, 112) * mm, "end": v(163, 97) * mm});
            skLineSegment(sketch, "E76.2.2.0", {"start": v(127, 85) * mm, "end": v(163, 85) * mm});
            skLineSegment(sketch, "E76.2.2.1", {"start": v(127, 70) * mm, "end": v(163, 70) * mm});
            skLineSegment(sketch, "E76.2.2.2", {"start": v(127, 85) * mm, "end": v(127, 70) * mm});
            skLineSegment(sketch, "E76.2.2.3", {"start": v(163, 85) * mm, "end": v(163, 70) * mm});
            skLineSegment(sketch, "E76.2.3.0", {"start": v(127, 58) * mm, "end": v(163, 58) * mm});
            skLineSegment(sketch, "E76.2.3.1", {"start": v(127, 43) * mm, "end": v(163, 43) * mm});
            skLineSegment(sketch, "E76.2.3.2", {"start": v(127, 58) * mm, "end": v(127, 43) * mm});
            skLineSegment(sketch, "E76.2.3.3", {"start": v(163, 58) * mm, "end": v(163, 43) * mm});
            skLineSegment(sketch, "E76.2.4.0", {"start": v(127, 31) * mm, "end": v(163, 31) * mm});
            skLineSegment(sketch, "E76.2.4.1", {"start": v(127, 16) * mm, "end": v(163, 16) * mm});
            skLineSegment(sketch, "E76.2.4.2", {"start": v(127, 31) * mm, "end": v(127, 16) * mm});
            skLineSegment(sketch, "E76.2.4.3", {"start": v(163, 31) * mm, "end": v(163, 16) * mm});
            skLineSegment(sketch, "E76.direction1", {"start": v(37, 139) * mm, "end": v(82, 139) * mm, "construction": true});
            skLineSegment(sketch, "E76.direction2", {"start": v(37, 139) * mm, "end": v(37, 112) * mm, "construction": true});
            skLineSegment(sketch, "E77.bottom", {"start": v(92.5, 0) * mm, "end": v(107.5, 0) * mm});
            skLineSegment(sketch, "E77.top", {"start": v(92.5, 25) * mm, "end": v(107.5, 25) * mm});
            skLineSegment(sketch, "E77.left", {"start": v(92.5, 0) * mm, "end": v(92.5, 25) * mm});
            skLineSegment(sketch, "E77.right", {"start": v(107.5, 0) * mm, "end": v(107.5, 25) * mm});
            skSolve(sketch);
        }
        {
            var Q0;
            Q0 = qSketchRegion(id + "F22", true);
            extrude(context, id + "F23", {"entities" : qUnion([Q0]), "operationType" : NewBodyOperationType.REMOVE, "oppositeDirection" : true, "depth" : 3 * mm});
        }
        {
            var Q0;
            Q0=makeQuery(id+"F1.opExtrude","SWEPT_FACE",FACE,{"disambiguationData":[OSD([sQuery(id+"F0.wireOp",EDGE,"E0.left")])]});
            var sketch = newSketch(context, id + "F24", { "sketchPlane" : qUnion([Q0])});
            skLineSegment(sketch, "E78.bottom", {"start": v(90, 31) * mm, "end": v(110, 31) * mm});
            skLineSegment(sketch, "E78.top", {"start": v(90, 27) * mm, "end": v(110, 27) * mm});
            skLineSegment(sketch, "E78.left", {"start": v(90, 31) * mm, "end": v(90, 27) * mm});
            skLineSegment(sketch, "E78.right", {"start": v(110, 31) * mm, "end": v(110, 27) * mm});
            skSolve(sketch);
        }
        {
            var Q0;
            Q0 = qSketchRegion(id + "F24", true);
            extrude(context, id + "F25", {"entities" : qUnion([Q0]), "operationType" : NewBodyOperationType.ADD, "depth" : 10 * mm});
        }
        {
            var Q0;
            Q0=makeQuery(id+"F1.opExtrude","SWEPT_FACE",FACE,{"disambiguationData":[OSD([sQuery(id+"F0.wireOp",EDGE,"E0.bottom")])]});
            var sketch = newSketch(context, id + "F26", { "sketchPlane" : qUnion([Q0])});
            skLineSegment(sketch, "E79.bottom", {"start": v(-168.78, 139) * mm, "end": v(-148.78, 139) * mm});
            skLineSegment(sketch, "E79.top", {"start": v(-168.78, 124) * mm, "end": v(-148.78, 124) * mm});
            skLineSegment(sketch, "E79.left", {"start": v(-168.78, 139) * mm, "end": v(-168.78, 124) * mm});
            skLineSegment(sketch, "E79.right", {"start": v(-148.78, 139) * mm, "end": v(-148.78, 124) * mm});
            skLineSegment(sketch, "E80.bottom", {"start": v(-140.78, 139) * mm, "end": v(-130.78, 139) * mm});
            skLineSegment(sketch, "E80.top", {"start": v(-140.78, 124) * mm, "end": v(-130.78, 124) * mm});
            skLineSegment(sketch, "E80.left", {"start": v(-140.78, 139) * mm, "end": v(-140.78, 124) * mm});
            skLineSegment(sketch, "E80.right", {"start": v(-130.78, 139) * mm, "end": v(-130.78, 124) * mm});
            skLineSegment(sketch, "E81.0.1.0", {"start": v(-168.78, 112) * mm, "end": v(-148.78, 112) * mm});
            skLineSegment(sketch, "E81.0.1.1", {"start": v(-168.78, 112) * mm, "end": v(-168.78, 97) * mm});
            skLineSegment(sketch, "E81.0.1.2", {"start": v(-168.78, 97) * mm, "end": v(-148.78, 97) * mm});
            skLineSegment(sketch, "E81.0.1.3", {"start": v(-148.78, 112) * mm, "end": v(-148.78, 97) * mm});
            skLineSegment(sketch, "E81.0.1.4", {"start": v(-140.78, 112) * mm, "end": v(-140.78, 97) * mm});
            skLineSegment(sketch, "E81.0.1.5", {"start": v(-140.78, 112) * mm, "end": v(-130.78, 112) * mm});
            skLineSegment(sketch, "E81.0.1.6", {"start": v(-130.78, 112) * mm, "end": v(-130.78, 97) * mm});
            skLineSegment(sketch, "E81.0.1.7", {"start": v(-140.78, 97) * mm, "end": v(-130.78, 97) * mm});
            skLineSegment(sketch, "E81.0.2.0", {"start": v(-168.78, 85) * mm, "end": v(-148.78, 85) * mm});
            skLineSegment(sketch, "E81.0.2.1", {"start": v(-168.78, 85) * mm, "end": v(-168.78, 70) * mm});
            skLineSegment(sketch, "E81.0.2.2", {"start": v(-168.78, 70) * mm, "end": v(-148.78, 70) * mm});
            skLineSegment(sketch, "E81.0.2.3", {"start": v(-148.78, 85) * mm, "end": v(-148.78, 70) * mm});
            skLineSegment(sketch, "E81.0.2.4", {"start": v(-140.78, 85) * mm, "end": v(-140.78, 70) * mm});
            skLineSegment(sketch, "E81.0.2.5", {"start": v(-140.78, 85) * mm, "end": v(-130.78, 85) * mm});
            skLineSegment(sketch, "E81.0.2.6", {"start": v(-130.78, 85) * mm, "end": v(-130.78, 70) * mm});
            skLineSegment(sketch, "E81.0.2.7", {"start": v(-140.78, 70) * mm, "end": v(-130.78, 70) * mm});
            skLineSegment(sketch, "E81.0.3.0", {"start": v(-168.78, 58) * mm, "end": v(-148.78, 58) * mm});
            skLineSegment(sketch, "E81.0.3.1", {"start": v(-168.78, 58) * mm, "end": v(-168.78, 43) * mm});
            skLineSegment(sketch, "E81.0.3.2", {"start": v(-168.78, 43) * mm, "end": v(-148.78, 43) * mm});
            skLineSegment(sketch, "E81.0.3.3", {"start": v(-148.78, 58) * mm, "end": v(-148.78, 43) * mm});
            skLineSegment(sketch, "E81.0.3.4", {"start": v(-140.78, 58) * mm, "end": v(-140.78, 43) * mm});
            skLineSegment(sketch, "E81.0.3.5", {"start": v(-140.78, 58) * mm, "end": v(-130.78, 58) * mm});
            skLineSegment(sketch, "E81.0.3.6", {"start": v(-130.78, 58) * mm, "end": v(-130.78, 43) * mm});
            skLineSegment(sketch, "E81.0.3.7", {"start": v(-140.78, 43) * mm, "end": v(-130.78, 43) * mm});
            skLineSegment(sketch, "E81.0.4.0", {"start": v(-168.78, 31) * mm, "end": v(-148.78, 31) * mm});
            skLineSegment(sketch, "E81.0.4.1", {"start": v(-168.78, 31) * mm, "end": v(-168.78, 16) * mm});
            skLineSegment(sketch, "E81.0.4.2", {"start": v(-168.78, 16) * mm, "end": v(-148.78, 16) * mm});
            skLineSegment(sketch, "E81.0.4.3", {"start": v(-148.78, 31) * mm, "end": v(-148.78, 16) * mm});
            skLineSegment(sketch, "E81.0.4.4", {"start": v(-140.78, 31) * mm, "end": v(-140.78, 16) * mm});
            skLineSegment(sketch, "E81.0.4.5", {"start": v(-140.78, 31) * mm, "end": v(-130.78, 31) * mm});
            skLineSegment(sketch, "E81.0.4.6", {"start": v(-130.78, 31) * mm, "end": v(-130.78, 16) * mm});
            skLineSegment(sketch, "E81.0.4.7", {"start": v(-140.78, 16) * mm, "end": v(-130.78, 16) * mm});
            skLineSegment(sketch, "E81.direction1", {"start": v(-168.78, 139) * mm, "end": v(-143.78, 139) * mm, "construction": true});
            skLineSegment(sketch, "E81.direction2", {"start": v(-168.78, 139) * mm, "end": v(-168.78, 112) * mm, "construction": true});
            skSolve(sketch);
        }
        {
            var Q0;
            Q0 = qSketchRegion(id + "F26", true);
            extrude(context, id + "F27", {"entities" : qUnion([Q0]), "operationType" : NewBodyOperationType.REMOVE, "oppositeDirection" : true, "depth" : 3 * mm});
        }
    });
